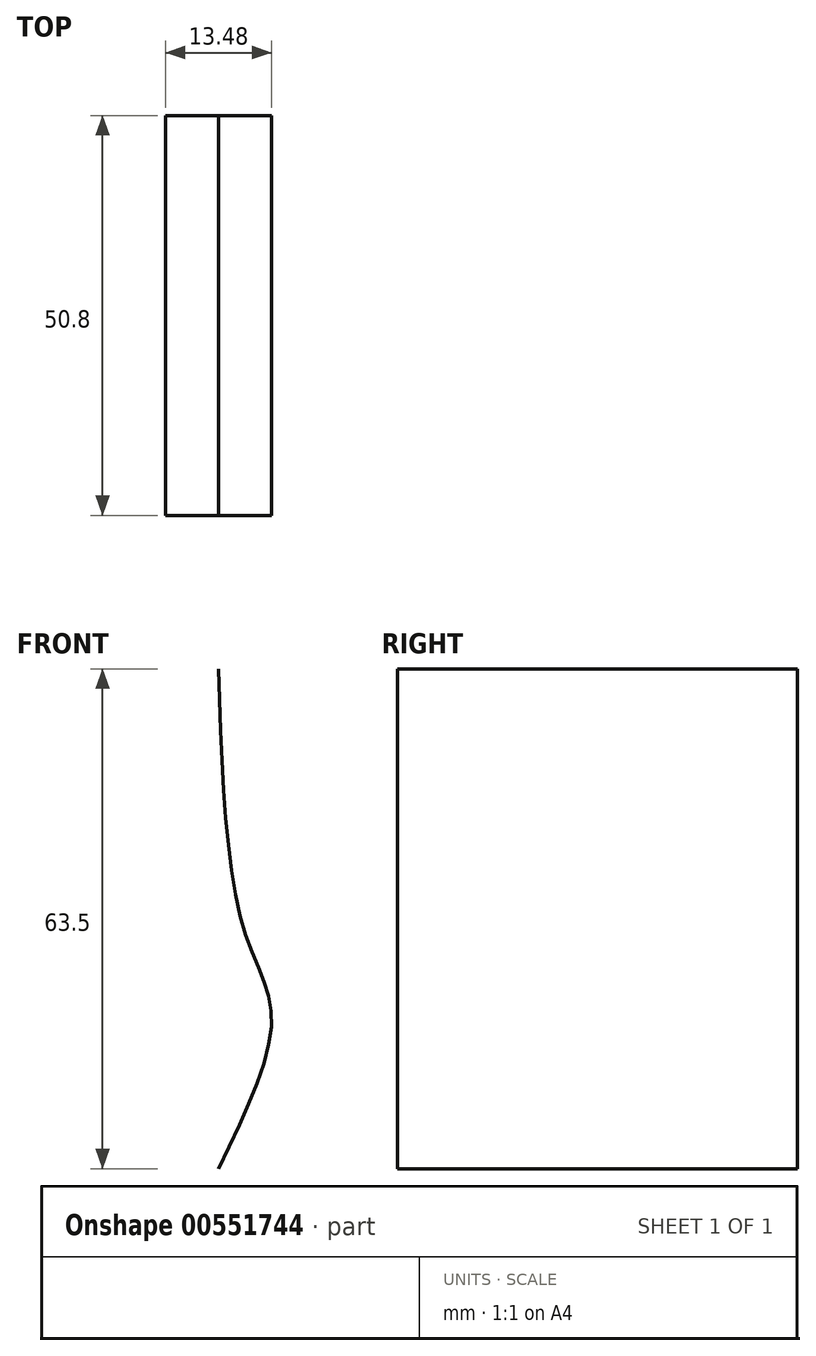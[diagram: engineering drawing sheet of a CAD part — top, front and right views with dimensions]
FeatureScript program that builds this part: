
annotation { "Feature Type Name" : "Feature", "Feature Type Description" : "" }
export const myFeature = defineFeature(function(context is Context, id is Id, definition is map)
    precondition{}
    {
        {
            var Q0;
            Q0=qCreatedBy(makeId("Front.planeOp"),FACE);
            var sketch = newSketch(context, id + "F0", { "sketchPlane" : qUnion([Q0])});
            skFitSpline(sketch, "E0", {"points": [v(0, 44.34) * mm, v(-3.19, 11.32) * mm, v(-6.74, 0) * mm, v(0, -19.16) * mm], "startDerivative": vector(-3, -90.48) * mm, "endDerivative": vector(31.11, -64.04) * mm});
            skFitSpline(sketch, "E1.MirrorCS", {"points": [v(0, 44.34) * mm, v(3.19, 11.32) * mm, v(6.74, 0) * mm, v(0, -19.16) * mm], "startDerivative": vector(3, -90.48) * mm, "endDerivative": vector(-31.11, -64.04) * mm});
            skSolve(sketch);
        }
        {
            var Q0;
            Q0=makeQuery(id+"F0.imprint","IMPRINT",FACE,{"disambiguationData":[TD([[makeQuery(id+"F0.imprint","IMPRINT",EDGE,{"derivedFrom":sQuery(id+"F0.wireOp",EDGE,"E0")}),1.0]])]});
            extrude(context, id + "F1", {"entities" : qUnion([Q0]), "endBound" : BoundingType.SYMMETRIC, "depth" : 50.8 * mm, "offsetDistance" : 25.4 * mm});
        }
    });
